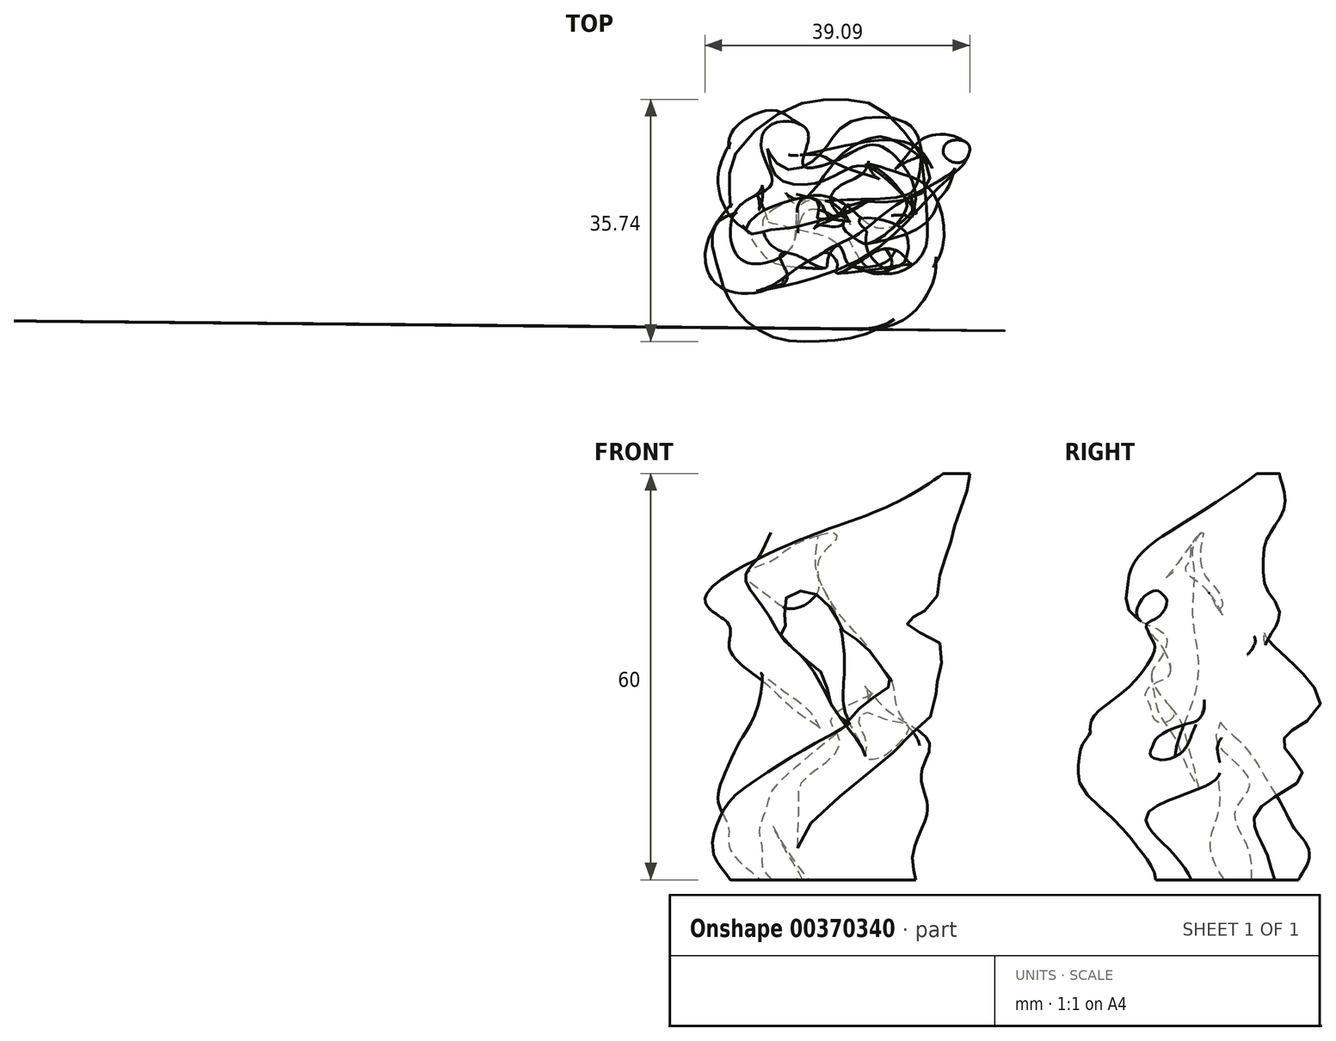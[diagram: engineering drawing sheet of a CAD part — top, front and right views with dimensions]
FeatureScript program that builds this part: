
annotation { "Feature Type Name" : "Feature", "Feature Type Description" : "" }
export const myFeature = defineFeature(function(context is Context, id is Id, definition is map)
    precondition{}
    {
        {
            var Q0;
            Q0=qCreatedBy(makeId("Top.planeOp"),FACE);
            cPlane(context, id + "F0", {"entities" : qUnion([Q0]), "cplaneType" : CPlaneType.OFFSET, "offset" : 5 * mm, "width" : 152.4 * mm, "height" : 152.4 * mm});
        }
        {
            var Q0;
            Q0=qCreatedBy(id+"F0.planeOp",FACE);
            var sketch = newSketch(context, id + "F1", { "sketchPlane" : qUnion([Q0])});
            skFitSpline(sketch, "E0", {"points": [v(-7.96, 10.3) * mm, v(-13.09, 11.46) * mm, v(-14.74, 7.49) * mm, v(-13.25, 2.69) * mm, v(-17.23, 0) * mm, v(-19.38, -3.93) * mm, v(-17.23, -8.9) * mm, v(-10.11, -6.41) * mm, v(-9.12, 0) * mm, v(-3.16, 0) * mm, v(2.63, -3.93) * mm, v(7.93, 0) * mm, v(2.8, 8.15) * mm, v(-2.83, 6.5) * mm, v(-8.62, 5.34) * mm, v(-7.96, 10.3) * mm]});
            skSolve(sketch);
        }
        {
            var Q0;
            Q0=qCreatedBy(id+"F0.planeOp",FACE);
            cPlane(context, id + "F2", {"entities" : qUnion([Q0]), "cplaneType" : CPlaneType.OFFSET, "offset" : 5 * mm, "width" : 152.4 * mm, "height" : 152.4 * mm});
        }
        {
            var Q0;
            Q0=qCreatedBy(id+"F2.planeOp",FACE);
            var sketch = newSketch(context, id + "F3", { "sketchPlane" : qUnion([Q0])});
            skFitSpline(sketch, "E1", {"points": [v(-16.9, 12.29) * mm, v(-19.54, 8.81) * mm, v(-16.73, 4.34) * mm, v(-14.74, 1.37) * mm, v(-15.9, -1.78) * mm, v(-21.2, -3.43) * mm, v(-21.53, -8.07) * mm, v(-16.23, -11.87) * mm, v(-10.11, -10.38) * mm, v(-9.45, -5.42) * mm, v(-7.8, -1.28) * mm, v(-3.32, -2.94) * mm, v(-1.67, -5.59) * mm, v(5.28, -7.57) * mm, v(7.76, -3.6) * mm, v(6.27, 2.52) * mm, v(0, 6.66) * mm, v(-5.15, 4.84) * mm, v(-11.1, 5.17) * mm, v(-11.43, 9.8) * mm, v(-12.92, 12.95) * mm, v(-16.9, 12.29) * mm]});
            skSolve(sketch);
        }
        {
            var Q0;
            Q0=qCreatedBy(id+"F2.planeOp",FACE);
            cPlane(context, id + "F4", {"entities" : qUnion([Q0]), "cplaneType" : CPlaneType.OFFSET, "offset" : 5 * mm, "width" : 152.4 * mm, "height" : 152.4 * mm});
        }
        {
            var Q0;
            Q0=qCreatedBy(id+"F4.planeOp",FACE);
            var sketch = newSketch(context, id + "F5", { "sketchPlane" : qUnion([Q0])});
            skFitSpline(sketch, "E2", {"points": [v(-17.56, 8.65) * mm, v(-20.54, 6.33) * mm, v(-19.54, 3.19) * mm, v(-16.56, 1.37) * mm, v(-14.25, -1.94) * mm, v(-15.74, -5.75) * mm, v(-18.05, -6.74) * mm, v(-20.04, -9.4) * mm, v(-20.2, -13.03) * mm, v(-15.24, -16.18) * mm, v(-8.79, -16.18) * mm, v(-5.97, -14.03) * mm, v(-6.47, -9.89) * mm, v(-9.28, -3.1) * mm, v(-6.8, 0) * mm, v(-2.33, -2.1) * mm, v(0, -8.4) * mm, v(4.62, -10.22) * mm, v(9.58, -6.25) * mm, v(7.6, 0) * mm, v(4.78, 2.69) * mm, v(0, 5.67) * mm, v(-5.97, 3.02) * mm, v(-12.92, 4.18) * mm, v(-14.25, 9.8) * mm, v(-17.56, 8.65) * mm]});
            skSolve(sketch);
        }
        {
            var Q0;
            Q0=qCreatedBy(id+"F4.planeOp",FACE);
            cPlane(context, id + "F6", {"entities" : qUnion([Q0]), "cplaneType" : CPlaneType.OFFSET, "offset" : 5 * mm, "width" : 152.4 * mm, "height" : 152.4 * mm});
        }
        {
            var Q0;
            Q0=qCreatedBy(id+"F6.planeOp",FACE);
            var sketch = newSketch(context, id + "F7", { "sketchPlane" : qUnion([Q0])});
            skFitSpline(sketch, "E3", {"points": [v(-17.06, 5.5) * mm, v(-20.37, 1.7) * mm, v(-19.54, -1.94) * mm, v(-16.4, -3.76) * mm, v(-12.92, -3.27) * mm, v(-11.6, -6.41) * mm, v(-13.75, -10.72) * mm, v(-15.08, -16.84) * mm, v(-11.27, -20.48) * mm, v(-6.47, -19.82) * mm, v(-4.15, -18.33) * mm, v(0, -13.03) * mm, v(-3.82, -7.07) * mm, v(-8.29, -1.28) * mm, v(-5.64, 0) * mm, v(-1.5, 0) * mm, v(4.95, 0) * mm, v(7.76, 1.7) * mm, v(8.6, 8.48) * mm, v(5.78, 11.8) * mm, v(-1.84, 11.63) * mm, v(-4.65, 8.81) * mm, v(-8.29, 5.17) * mm, v(-11.6, 4.84) * mm, v(-14.08, 7) * mm, v(-17.06, 5.5) * mm]});
            skSolve(sketch);
        }
        {
            var Q0;
            Q0=qCreatedBy(id+"F6.planeOp",FACE);
            var sketch = newSketch(context, id + "F8", { "sketchPlane" : qUnion([Q0])});
            skFitSpline(sketch, "E4", {"points": [v(1.3, -6.46) * mm, v(-0.9, -5.42) * mm, v(-1.04, -3.29) * mm, v(0.75, -1.77) * mm, v(2.96, -1.02) * mm, v(5.5, -0.8) * mm, v(7.5, -1.7) * mm, v(8.54, -3.43) * mm, v(8.4, -5.42) * mm, v(6.75, -6.87) * mm, v(4.2, -7.5) * mm, v(2.06, -6.94) * mm, v(1.3, -6.46) * mm]});
            skSolve(sketch);
        }
        {
            var Q0;
            Q0=qCreatedBy(id+"F6.planeOp",FACE);
            cPlane(context, id + "F9", {"entities" : qUnion([Q0]), "cplaneType" : CPlaneType.OFFSET, "offset" : 5 * mm, "width" : 152.4 * mm, "height" : 152.4 * mm});
        }
        {
            var Q0;
            Q0=qCreatedBy(id+"F9.planeOp",FACE);
            var sketch = newSketch(context, id + "F10", { "sketchPlane" : qUnion([Q0])});
            skFitSpline(sketch, "E5", {"points": [v(-17.4, 0) * mm, v(-18.22, -1.94) * mm, v(-16.73, -4.43) * mm, v(-13.25, -5.92) * mm, v(-10.77, -5.25) * mm, v(-7.46, -4.6) * mm, v(-5.8, -7.4) * mm, v(-6.14, -10.72) * mm, v(-6.97, -14.03) * mm, v(-6.63, -18.16) * mm, v(-4.81, -19.16) * mm, v(-2, -19.98) * mm, v(1.97, -19) * mm, v(4.78, -16.5) * mm, v(5.78, -11.05) * mm, v(3.13, -6.08) * mm, v(0, -4.1) * mm, v(-3.16, -1.61) * mm, v(0, 0) * mm, v(4.45, 0) * mm, v(9.58, 2.03) * mm, v(9.92, 4.68) * mm, v(8.76, 6.5) * mm, v(4.29, 9.3) * mm, v(1.8, 9.48) * mm, v(-1.34, 8.15) * mm, v(-4.15, 5.67) * mm, v(-6.47, 2.69) * mm, v(-10.11, 0) * mm, v(-11.6, 1.86) * mm, v(-15.24, 3.52) * mm, v(-17.4, 0) * mm]});
            skSolve(sketch);
        }
        {
            var Q0;
            Q0=qCreatedBy(id+"F9.planeOp",FACE);
            var sketch = newSketch(context, id + "F11", { "sketchPlane" : qUnion([Q0])});
            skFitSpline(sketch, "E6", {"points": [v(7.32, -8.62) * mm, v(4.71, -9.83) * mm, v(1.7, -10.43) * mm, v(0, -8.42) * mm, v(0, -5.82) * mm, v(1.7, -3.6) * mm, v(4.51, -2.6) * mm, v(7.92, -3.4) * mm, v(8.52, -5.41) * mm, v(8.32, -6.82) * mm, v(7.32, -8.62) * mm]});
            skSolve(sketch);
        }
        {
            var Q0;
            Q0=qCreatedBy(id+"F9.planeOp",FACE);
            cPlane(context, id + "F12", {"entities" : qUnion([Q0]), "cplaneType" : CPlaneType.OFFSET, "offset" : 5 * mm, "width" : 152.4 * mm, "height" : 152.4 * mm});
        }
        {
            var Q0;
            Q0=qCreatedBy(id+"F12.planeOp",FACE);
            var sketch = newSketch(context, id + "F13", { "sketchPlane" : qUnion([Q0])});
            skFitSpline(sketch, "E7", {"points": [v(-15.08, -2.77) * mm, v(-14.9, -7.24) * mm, v(-12.76, -8.9) * mm, v(-8.62, -7.9) * mm, v(-5.31, -6.58) * mm, v(-2.33, -7.57) * mm, v(0, -11.54) * mm, v(1.3, -16.01) * mm, v(5.61, -17.5) * mm, v(9.25, -14.36) * mm, v(10.74, -9.89) * mm, v(8.76, -3.43) * mm, v(4.78, -2.1) * mm, v(-1.34, -1.78) * mm, v(-3.32, 1.7) * mm, v(0, 4.01) * mm, v(1.47, 6.33) * mm, v(3.63, 9.64) * mm, v(2.8, 13.61) * mm, v(-3.5, 14.77) * mm, v(-7.46, 13.78) * mm, v(-9.78, 10.47) * mm, v(-7.96, 6.33) * mm, v(-8.62, 2.03) * mm, v(-10.77, 0) * mm, v(-15.08, -2.77) * mm]});
            skSolve(sketch);
        }
        {
            var Q0;
            Q0=qCreatedBy(id+"F12.planeOp",FACE);
            var sketch = newSketch(context, id + "F14", { "sketchPlane" : qUnion([Q0])});
            skFitSpline(sketch, "E8", {"points": [v(0, -9.83) * mm, v(-3.3, -8.82) * mm, v(-3.91, -6.62) * mm, v(-2.5, -4.21) * mm, v(0, -2.4) * mm, v(5.11, -4.81) * mm, v(4.91, -7.42) * mm, v(3.5, -9.02) * mm, v(0, -9.83) * mm]});
            skSolve(sketch);
        }
        {
            var Q0;
            Q0=qCreatedBy(id+"F12.planeOp",FACE);
            cPlane(context, id + "F15", {"entities" : qUnion([Q0]), "cplaneType" : CPlaneType.OFFSET, "offset" : 5 * mm, "width" : 152.4 * mm, "height" : 152.4 * mm});
        }
        {
            var Q0;
            Q0=qCreatedBy(id+"F15.planeOp",FACE);
            var sketch = newSketch(context, id + "F16", { "sketchPlane" : qUnion([Q0])});
            skFitSpline(sketch, "E9", {"points": [v(8.51, -11.76) * mm, v(10.62, -9.65) * mm, v(11.32, -6.5) * mm, v(10.62, -1.58) * mm, v(7.63, 0) * mm, v(4.12, 2.63) * mm, v(0, 4.91) * mm, v(-1.5, 9.65) * mm, v(-5.18, 12.28) * mm, v(-13.78, 11.93) * mm, v(-15.35, 6.32) * mm, v(-14.3, 1.93) * mm, v(-14.65, -2.63) * mm, v(-12.9, -8.07) * mm, v(-7.63, -9.83) * mm, v(-3.07, -9.3) * mm, v(3.77, -7.37) * mm, v(6.23, -10.18) * mm, v(8.51, -11.76) * mm]});
            skSolve(sketch);
        }
        {
            var Q0;
            Q0=qCreatedBy(id+"F15.planeOp",FACE);
            var sketch = newSketch(context, id + "F17", { "sketchPlane" : qUnion([Q0])});
            skFitSpline(sketch, "E10", {"points": [v(-3.5, -11.03) * mm, v(-6.52, -8.42) * mm, v(-5.31, -4.81) * mm, v(-3.1, -3) * mm, v(0, -3.4) * mm, v(3.1, -5.41) * mm, v(3.91, -7.82) * mm, v(3.91, -10.03) * mm, v(2.3, -12.03) * mm, v(0, -12.63) * mm, v(-3.5, -11.03) * mm]});
            skSolve(sketch);
        }
        {
            var Q0;
            Q0=qCreatedBy(id+"F15.planeOp",FACE);
            cPlane(context, id + "F18", {"entities" : qUnion([Q0]), "cplaneType" : CPlaneType.OFFSET, "offset" : 5 * mm, "width" : 152.4 * mm, "height" : 152.4 * mm});
        }
        {
            var Q0;
            Q0=qCreatedBy(id+"F18.planeOp",FACE);
            var sketch = newSketch(context, id + "F19", { "sketchPlane" : qUnion([Q0])});
            skFitSpline(sketch, "E11", {"points": [v(-18.22, 6.1) * mm, v(-19.54, 2.84) * mm, v(-18.13, -2.86) * mm, v(-13.66, -6.81) * mm, v(-8.48, -7.78) * mm, v(-4.7, -7.69) * mm, v(-3.38, -7.95) * mm, v(4.08, -9.45) * mm, v(5.48, -9.45) * mm, v(10.4, -7.51) * mm, v(10.13, 1.53) * mm, v(5.48, 4.16) * mm, v(1.1, 5.48) * mm, v(0, 5.3) * mm, v(-4.61, 6.88) * mm, v(-6.02, 7.06) * mm, v(-9.44, 6.88) * mm, v(-11.11, 7.06) * mm, v(-15.06, 7.76) * mm, v(-18.22, 6.1) * mm]});
            skSolve(sketch);
        }
        {
            var Q0;
            Q0=qCreatedBy(id+"F18.planeOp",FACE);
            var sketch = newSketch(context, id + "F20", { "sketchPlane" : qUnion([Q0])});
            skFitSpline(sketch, "E12", {"points": [v(-2.1, -10.63) * mm, v(-5.11, -13.23) * mm, v(-7.12, -12.43) * mm, v(-10.53, -9.42) * mm, v(-10.93, -6.82) * mm, v(-8.52, -3.4) * mm, v(-5.31, -2.4) * mm, v(0, -5.41) * mm, v(0, -8.62) * mm, v(-2.1, -10.63) * mm]});
            skSolve(sketch);
        }
        {
            var Q0;
            Q0=qCreatedBy(id+"F18.planeOp",FACE);
            cPlane(context, id + "F21", {"entities" : qUnion([Q0]), "cplaneType" : CPlaneType.OFFSET, "offset" : 5 * mm, "width" : 152.4 * mm, "height" : 152.4 * mm});
        }
        {
            var Q0;
            Q0=qCreatedBy(id+"F21.planeOp",FACE);
            var sketch = newSketch(context, id + "F22", { "sketchPlane" : qUnion([Q0])});
            skFitSpline(sketch, "E13", {"points": [v(-5.31, -8.23) * mm, v(-1.34, -6.9) * mm, v(2.63, -5.75) * mm, v(7.6, -3.76) * mm, v(9.42, -1.28) * mm, v(9.58, 3.68) * mm, v(8.1, 7.65) * mm, v(5.28, 8.98) * mm, v(0, 7.82) * mm, v(-3.99, 5.34) * mm, v(-8.29, 1.53) * mm, v(-11.6, 0) * mm, v(-18.05, 0) * mm, v(-21.7, -3.93) * mm, v(-22.36, -8.23) * mm, v(-20.04, -11.87) * mm, v(-14.9, -13.2) * mm, v(-9.94, -11.05) * mm, v(-7.3, -9.56) * mm, v(-5.31, -8.23) * mm]});
            skSolve(sketch);
        }
        {
            var Q0;
            Q0=qCreatedBy(id+"F21.planeOp",FACE);
            var sketch = newSketch(context, id + "F23", { "sketchPlane" : qUnion([Q0])});
            skFitSpline(sketch, "E14", {"points": [v(-4.71, -8.42) * mm, v(-6.92, -11.23) * mm, v(-9.93, -12.03) * mm, v(-12.33, -11.63) * mm, v(-13.54, -9.02) * mm, v(-14.34, -5.41) * mm, v(-12.93, -2.2) * mm, v(-10.93, 0) * mm, v(-6.52, 0) * mm, v(-5.31, -1.6) * mm, v(-3.91, -4.41) * mm, v(-4.71, -8.42) * mm]});
            skSolve(sketch);
        }
        {
            var Q0;
            Q0=qCreatedBy(id+"F21.planeOp",FACE);
            cPlane(context, id + "F24", {"entities" : qUnion([Q0]), "cplaneType" : CPlaneType.OFFSET, "offset" : 5 * mm, "width" : 152.4 * mm, "height" : 152.4 * mm});
        }
        {
            var Q0;
            Q0=qCreatedBy(id+"F24.planeOp",FACE);
            var sketch = newSketch(context, id + "F25", { "sketchPlane" : qUnion([Q0])});
            skFitSpline(sketch, "E15", {"points": [v(-5.31, -1.61) * mm, v(-9.12, -2.1) * mm, v(-11.27, -2.44) * mm, v(-15.9, -3.76) * mm, v(-19.54, -7.07) * mm, v(-18.22, -12.37) * mm, v(-11.77, -12.2) * mm, v(-6.63, -8.4) * mm, v(-2.83, -6.25) * mm, v(0, -4.6) * mm, v(3.96, -3.43) * mm, v(8.26, -1.94) * mm, v(11.24, 0) * mm, v(10.74, 4.84) * mm, v(8.26, 6.66) * mm, v(2.14, 5.17) * mm, v(-2, 1.7) * mm, v(-5.31, -1.61) * mm]});
            skSolve(sketch);
        }
        {
            var Q0;
            Q0=qCreatedBy(id+"F24.planeOp",FACE);
            var sketch = newSketch(context, id + "F26", { "sketchPlane" : qUnion([Q0])});
            skFitSpline(sketch, "E16", {"points": [v(-12.13, -7.22) * mm, v(-15.54, -7.02) * mm, v(-17.15, -4.21) * mm, v(-14.94, 0) * mm, v(-10.93, 2) * mm, v(-7.72, 0) * mm, v(-6.92, 0) * mm, v(-6.72, -4.61) * mm, v(-9.12, -7.22) * mm, v(-12.13, -7.22) * mm]});
            skSolve(sketch);
        }
        {
            var Q0;
            Q0=qCreatedBy(id+"F24.planeOp",FACE);
            cPlane(context, id + "F27", {"entities" : qUnion([Q0]), "cplaneType" : CPlaneType.OFFSET, "offset" : 5 * mm, "width" : 152.4 * mm, "height" : 152.4 * mm});
        }
        {
            var Q0;
            Q0=qCreatedBy(id+"F27.planeOp",FACE);
            var sketch = newSketch(context, id + "F28", { "sketchPlane" : qUnion([Q0])});
            skFitSpline(sketch, "E17", {"points": [v(11.53, 7.02) * mm, v(4.91, 4.81) * mm, v(-2.9, -2) * mm, v(-9.32, -4.01) * mm, v(-7.72, -8.02) * mm, v(0, -8.42) * mm, v(2.3, -3.81) * mm, v(6.32, 0) * mm, v(12.53, 1.8) * mm, v(12.93, 5.41) * mm, v(11.53, 7.02) * mm]});
            skSolve(sketch);
        }
        {
            var Q0;
            Q0=qCreatedBy(id+"F27.planeOp",FACE);
            var sketch = newSketch(context, id + "F29", { "sketchPlane" : qUnion([Q0])});
            skFitSpline(sketch, "E18", {"points": [v(-10.13, -3.2) * mm, v(-13.33, 0) * mm, v(-13.74, 3.4) * mm, v(-10.73, 5.41) * mm, v(-8.92, 6.22) * mm, v(-4.31, 4.41) * mm, v(-2.5, 0) * mm, v(-3.7, -2.2) * mm, v(-6.52, -3.4) * mm, v(-10.13, -3.2) * mm]});
            skSolve(sketch);
        }
        {
            var Q0;
            Q0=qCreatedBy(id+"F27.planeOp",FACE);
            cPlane(context, id + "F30", {"entities" : qUnion([Q0]), "cplaneType" : CPlaneType.OFFSET, "offset" : 5 * mm, "width" : 152.4 * mm, "height" : 152.4 * mm});
        }
        {
            var Q0;
            Q0=qCreatedBy(id+"F30.planeOp",FACE);
            var sketch = newSketch(context, id + "F31", { "sketchPlane" : qUnion([Q0])});
            skFitSpline(sketch, "E19", {"points": [v(3.58, 0) * mm, v(5.32, -1.45) * mm, v(9.3, 0) * mm, v(12.42, 3.23) * mm, v(14.5, 5.48) * mm, v(13.8, 8.95) * mm, v(9.13, 9.3) * mm, v(6.36, 5.48) * mm, v(4.8, 2.7) * mm, v(3.58, 0) * mm]});
            skSolve(sketch);
        }
        {
            var Q0;
            Q0=qCreatedBy(id+"F30.planeOp",FACE);
            var sketch = newSketch(context, id + "F32", { "sketchPlane" : qUnion([Q0])});
            skFitSpline(sketch, "E20", {"points": [v(-7.92, 2.4) * mm, v(-10.73, 5.82) * mm, v(-10.73, 8.82) * mm, v(-7.32, 11.43) * mm, v(-2.3, 9.83) * mm, v(0, 6.42) * mm, v(-1.9, 3.2) * mm, v(-5.11, 1.8) * mm, v(-7.92, 2.4) * mm]});
            skSolve(sketch);
        }
        {
            var Q0;
            Q0=qCreatedBy(id+"F30.planeOp",FACE);
            cPlane(context, id + "F33", {"entities" : qUnion([Q0]), "cplaneType" : CPlaneType.OFFSET, "offset" : 5 * mm, "width" : 152.4 * mm, "height" : 152.4 * mm});
        }
        {
            var Q0;
            Q0=qCreatedBy(id+"F33.planeOp",FACE);
            var sketch = newSketch(context, id + "F34", { "sketchPlane" : qUnion([Q0])});
            skFitSpline(sketch, "E21", {"points": [v(12.7, 8.71) * mm, v(12.23, 6.76) * mm, v(14.41, 5.74) * mm, v(15.83, 7) * mm, v(15.57, 8.63) * mm, v(12.7, 8.71) * mm]});
            skSolve(sketch);
        }
        {
            var Q0;
            Q0 = qSketchRegion(id + "F1", true);
            var Q1;
            Q1 = qSketchRegion(id + "F3", true);
            var Q2;
            Q2 = qSketchRegion(id + "F5", true);
            var Q3;
            Q3 = qSketchRegion(id + "F7", true);
            var Q4;
            Q4 = qSketchRegion(id + "F10", true);
            var Q5;
            Q5 = qSketchRegion(id + "F13", true);
            var Q6;
            Q6 = qSketchRegion(id + "F16", true);
            var Q7;
            Q7 = qSketchRegion(id + "F19", true);
            var Q8;
            Q8 = qSketchRegion(id + "F22", true);
            var Q9;
            Q9 = qSketchRegion(id + "F25", true);
            var Q10;
            Q10 = qSketchRegion(id + "F28", true);
            var Q11;
            Q11 = qSketchRegion(id + "F31", true);
            var Q12;
            Q12 = qSketchRegion(id + "F34", true);
            loft(context, id + "F35", {"sheetProfilesArray" : [{ "sheetProfileEntities" : qUnion([Q0]) }, { "sheetProfileEntities" : qUnion([Q1]) }, { "sheetProfileEntities" : qUnion([Q2]) }, { "sheetProfileEntities" : qUnion([Q3]) }, { "sheetProfileEntities" : qUnion([Q4]) }, { "sheetProfileEntities" : qUnion([Q5]) }, { "sheetProfileEntities" : qUnion([Q6]) }, { "sheetProfileEntities" : qUnion([Q7]) }, { "sheetProfileEntities" : qUnion([Q8]) }, { "sheetProfileEntities" : qUnion([Q9]) }, { "sheetProfileEntities" : qUnion([Q10]) }, { "sheetProfileEntities" : qUnion([Q11]) }, { "sheetProfileEntities" : qUnion([Q12]) }]});
        }
        {
            var Q1;
            Q1 = qSketchRegion(id + "F8", true);
            var Q2;
            Q2 = qSketchRegion(id + "F11", true);
            var Q3;
            Q3 = qSketchRegion(id + "F14", true);
            var Q4;
            Q4 = qSketchRegion(id + "F17", true);
            var Q5;
            Q5 = qSketchRegion(id + "F20", true);
            var Q6;
            Q6 = qSketchRegion(id + "F23", true);
            var Q7;
            Q7 = qSketchRegion(id + "F26", true);
            var Q8;
            Q8 = qSketchRegion(id + "F29", true);
            var Q9;
            Q9 = qSketchRegion(id + "F32", true);
            loft(context, id + "F36", {"operationType" : NewBodyOperationType.REMOVE, "sheetProfilesArray" : [{ "sheetProfileEntities" : qUnion([Q1]) }, { "sheetProfileEntities" : qUnion([Q2]) }, { "sheetProfileEntities" : qUnion([Q3]) }, { "sheetProfileEntities" : qUnion([Q4]) }, { "sheetProfileEntities" : qUnion([Q5]) }, { "sheetProfileEntities" : qUnion([Q6]) }, { "sheetProfileEntities" : qUnion([Q7]) }, { "sheetProfileEntities" : qUnion([Q8]) }, { "sheetProfileEntities" : qUnion([Q9]) }]});
        }
    });
